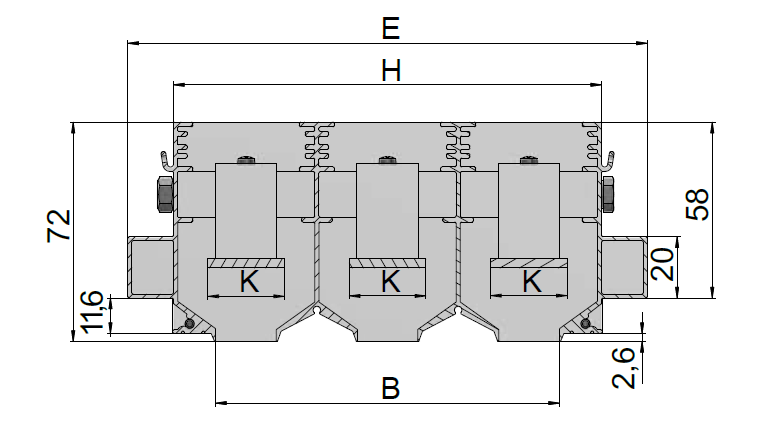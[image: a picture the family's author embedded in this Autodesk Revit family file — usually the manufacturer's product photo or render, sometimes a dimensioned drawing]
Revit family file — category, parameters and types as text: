
# Revit family: GR_Адаптер линейный_Муфта(n)_АДЛ-КСД-У_О_R21
name_source: partatom
category: Соединительные детали воздуховодов
units: mm (PartAtom-declared; Revit-internal decimal feet)

## family parameters
Всегда вертикально = Да
Заголовок OmniClass = Metal Ducts
На основе рабочей плоскости = Нет
Номер OmniClass = 23.75.70.14.31
Общий = Нет
При загрузке вырезать с полостями = Нет
Размер круглого соединителя = Использовать диаметр
Тип детали = Мультипорт

## types (6) — shared parameters
ADSK_URL страницы изделия = https://grilles.ru
ADSK_Версия Revit = 2021
ADSK_Единица измерения = шт.
ADSK_Завод-изготовитель = ООО "ВЕНТРЕШЕТКИКОМ"
ADSK_Код изделия = 002010
ADSK_Количество = 1
ADSK_Материал = ADSK_Оцинкованная сталь
ADSK_Наименование = АДЛ-КСД-У-О, адаптер вентиляционной решётки радиальный
Изготовитель = ООО "ВЕНТРЕШЕТКИКОМ"
Корпус_Металл_Толщина = 1 мм
Муфта_Металл_Толщина = 1 мм
zero-valued in all types: Отметка по умолчанию

## per-type parameters (varying)
| type | Корпус_Высота | Корпус_Длина | Решетка_отступ | Решётка_Высота |
| АДЛ-КСД-У-О 1-20 | 130 мм | 171 мм | 25 мм | 48 мм |
| АДЛ-КСД-У-О 2-20 | 130 мм | 209 мм | 44 мм | 86 мм |
| АДЛ-КСД-У-О 3-20 | 130 мм | 247 мм | 63 мм | 124 мм |
| АДЛ-КСД-У-О 4-20 | 170 мм | 285 мм | 82 мм | 162 мм |
| АДЛ-КСД-У-О 5-20 | 170 мм | 323 мм | 101 мм | 200 мм |
| АДЛ-КСД-У-О 6-20 | 170 мм | 361 мм | 120 мм | 238 мм |

note: column(s) folded — value = type name in every type: ADSK_Марка
